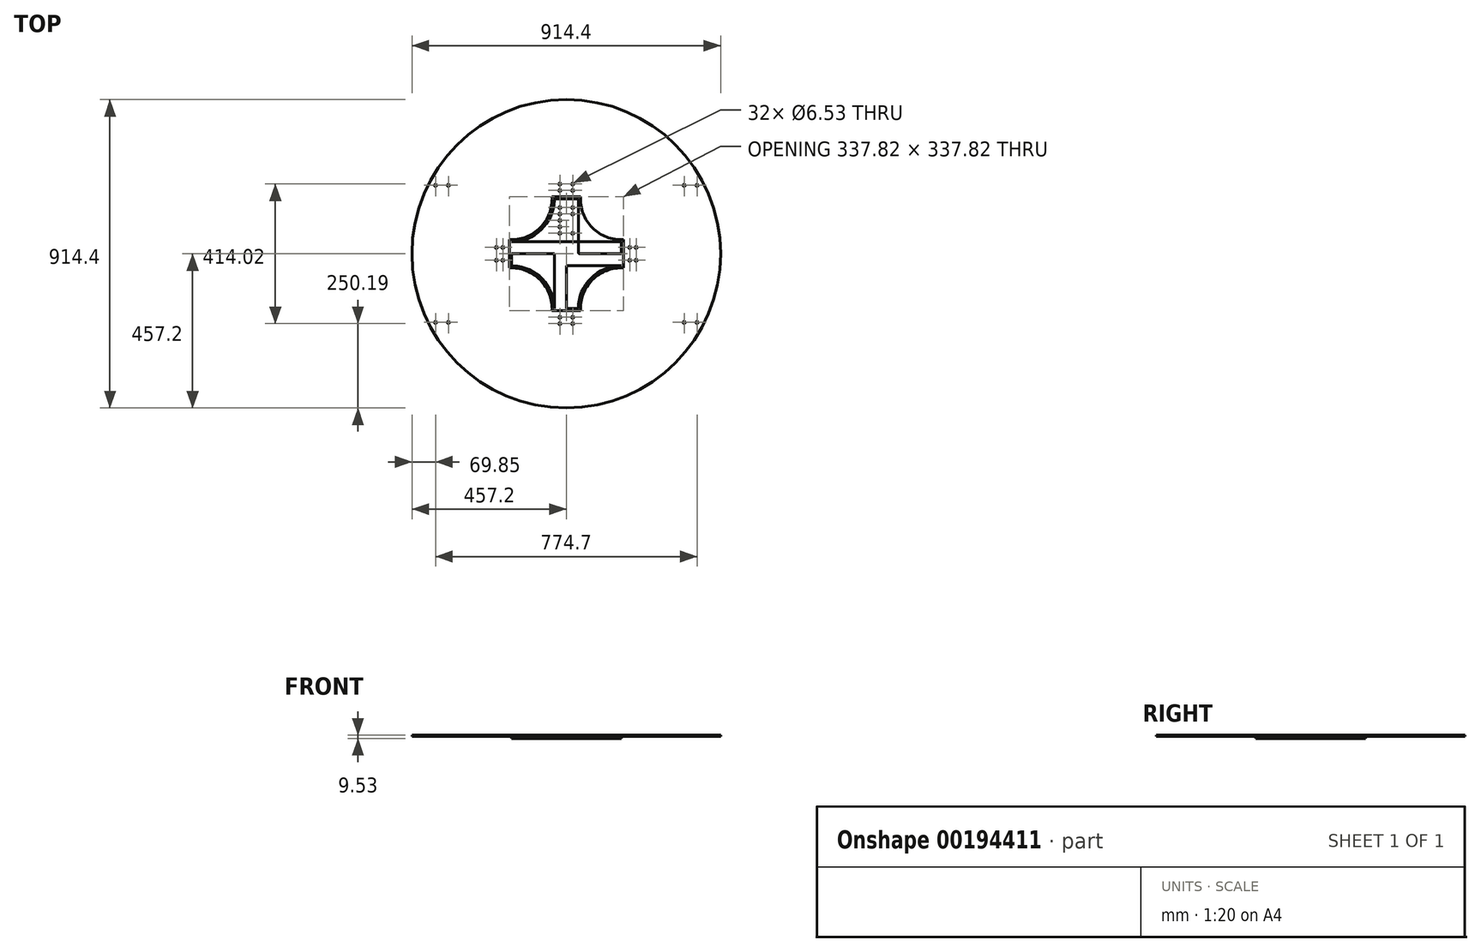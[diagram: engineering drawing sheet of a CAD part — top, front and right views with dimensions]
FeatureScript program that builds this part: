
annotation { "Feature Type Name" : "Feature", "Feature Type Description" : "" }
export const myFeature = defineFeature(function(context is Context, id is Id, definition is map)
    precondition{}
    {
        {
            var Q0;
            Q0=qCreatedBy(makeId("Top.planeOp"),FACE);
            var sketch = newSketch(context, id + "F0", { "sketchPlane" : qUnion([Q0])});
            skLineSegment(sketch, "E0.bottom", {"start": v(35.56, -35.56) * mm, "end": v(-35.56, -35.56) * mm});
            skLineSegment(sketch, "E0.top", {"start": v(35.56, 35.56) * mm, "end": v(-35.56, 35.56) * mm});
            skLineSegment(sketch, "E0.left", {"start": v(35.56, -35.56) * mm, "end": v(35.56, 35.56) * mm});
            skLineSegment(sketch, "E0.right", {"start": v(-35.56, -35.56) * mm, "end": v(-35.56, 35.56) * mm});
            skPoint(sketch, "E0.middle", {"position": v(0, 0) * mm});
            skLineSegment(sketch, "E1", {"start": v(0, 35.56) * mm, "end": v(0, 162.56) * mm});
            skPoint(sketch, "E1.endSnap0", {"position": v(0, 35.56) * mm});
            skLineSegment(sketch, "E2", {"start": v(0, 162.56) * mm, "end": v(-35.56, 162.56) * mm});
            skLineSegment(sketch, "E3", {"start": v(0, 162.56) * mm, "end": v(35.56, 162.56) * mm});
            skLineSegment(sketch, "E4", {"start": v(-35.56, 162.56) * mm, "end": v(-35.56, 35.56) * mm});
            skLineSegment(sketch, "E5", {"start": v(35.56, 162.56) * mm, "end": v(35.56, 35.56) * mm});
            skLineSegment(sketch, "E6", {"start": v(-35.56, 35.56) * mm, "end": v(-162.56, 35.56) * mm});
            skLineSegment(sketch, "E7", {"start": v(-35.56, 35.56) * mm, "end": v(-53.52, 53.52) * mm});
            skArc(sketch, "E8", {"start": v(-162.56, 35.56) * mm, "mid": v(-72.76, 72.76) * mm, "end": v(-35.56, 162.56) * mm});
            skLineSegment(sketch, "E9", {"start": v(0, 35.56) * mm, "end": v(0, 60.96) * mm});
            skLineSegment(sketch, "E10", {"start": v(0, 60.96) * mm, "end": v(19.05, 60.96) * mm});
            skLineSegment(sketch, "E11", {"start": v(19.05, 60.96) * mm, "end": v(19.05, 80.01) * mm});
            skLineSegment(sketch, "E12", {"start": v(19.05, 80.01) * mm, "end": v(19.05, 99.06) * mm});
            skLineSegment(sketch, "E13", {"start": v(19.05, 99.06) * mm, "end": v(19.05, 118.11) * mm});
            skLineSegment(sketch, "E14", {"start": v(19.05, 118.11) * mm, "end": v(19.05, 137.16) * mm});
            skLineSegment(sketch, "E15", {"start": v(19.05, 137.16) * mm, "end": v(19.05, 156.21) * mm});
            skLineSegment(sketch, "E16.MirrorCS", {"start": v(-19.05, 60.96) * mm, "end": v(-19.05, 80.01) * mm});
            skLineSegment(sketch, "E17.MirrorCS", {"start": v(-19.05, 80.01) * mm, "end": v(-19.05, 99.06) * mm});
            skLineSegment(sketch, "E18.MirrorCS", {"start": v(0, 60.96) * mm, "end": v(-19.05, 60.96) * mm});
            skLineSegment(sketch, "E19.MirrorCS", {"start": v(-19.05, 99.06) * mm, "end": v(-19.05, 118.11) * mm});
            skLineSegment(sketch, "E20.MirrorCS", {"start": v(-19.05, 118.11) * mm, "end": v(-19.05, 137.16) * mm});
            skLineSegment(sketch, "E21.MirrorCS", {"start": v(-19.05, 137.16) * mm, "end": v(-19.05, 156.21) * mm});
            skLineSegment(sketch, "E22.1.0", {"start": v(-80.01, -19.05) * mm, "end": v(-99.06, -19.05) * mm});
            skLineSegment(sketch, "E22.1.1", {"start": v(-60.96, 19.05) * mm, "end": v(-80.01, 19.05) * mm});
            skLineSegment(sketch, "E22.1.2", {"start": v(-80.01, 19.05) * mm, "end": v(-99.06, 19.05) * mm});
            skLineSegment(sketch, "E22.1.3", {"start": v(-60.96, -19.05) * mm, "end": v(-80.01, -19.05) * mm});
            skLineSegment(sketch, "E22.1.4", {"start": v(-118.11, 19.05) * mm, "end": v(-137.16, 19.05) * mm});
            skLineSegment(sketch, "E22.1.5", {"start": v(-80.01, 19.05) * mm, "end": v(-99.06, 19.05) * mm});
            skLineSegment(sketch, "E22.1.6", {"start": v(-162.56, 35.56) * mm, "end": v(-35.56, 35.56) * mm});
            skLineSegment(sketch, "E22.1.7", {"start": v(-35.56, -35.56) * mm, "end": v(-53.52, -53.52) * mm});
            skLineSegment(sketch, "E22.1.8", {"start": v(-137.16, 19.05) * mm, "end": v(-156.21, 19.05) * mm});
            skLineSegment(sketch, "E22.1.9", {"start": v(-35.56, -35.56) * mm, "end": v(-35.56, -162.56) * mm});
            skLineSegment(sketch, "E22.1.10", {"start": v(-162.56, -35.56) * mm, "end": v(-35.56, -35.56) * mm});
            skArc(sketch, "E22.1.11", {"start": v(-35.56, -162.56) * mm, "mid": v(-72.76, -72.76) * mm, "end": v(-162.56, -35.56) * mm});
            skLineSegment(sketch, "E22.1.12", {"start": v(-99.06, -19.05) * mm, "end": v(-118.11, -19.05) * mm});
            skLineSegment(sketch, "E22.1.13", {"start": v(-99.06, 19.05) * mm, "end": v(-118.11, 19.05) * mm});
            skLineSegment(sketch, "E22.1.14", {"start": v(-60.96, 0) * mm, "end": v(-60.96, 19.05) * mm});
            skLineSegment(sketch, "E22.1.15", {"start": v(-162.56, 0) * mm, "end": v(-162.56, 35.56) * mm});
            skLineSegment(sketch, "E22.1.16", {"start": v(-35.56, 0) * mm, "end": v(-162.56, 0) * mm});
            skLineSegment(sketch, "E22.1.17", {"start": v(-162.56, 0) * mm, "end": v(-162.56, -35.56) * mm});
            skLineSegment(sketch, "E22.1.18", {"start": v(-60.96, 0) * mm, "end": v(-60.96, -19.05) * mm});
            skLineSegment(sketch, "E22.1.19", {"start": v(-35.56, 35.56) * mm, "end": v(-35.56, -35.56) * mm});
            skLineSegment(sketch, "E22.1.20", {"start": v(-137.16, -19.05) * mm, "end": v(-156.21, -19.05) * mm});
            skLineSegment(sketch, "E22.1.21", {"start": v(-35.56, 0) * mm, "end": v(-60.96, 0) * mm});
            skLineSegment(sketch, "E22.1.22", {"start": v(-118.11, -19.05) * mm, "end": v(-137.16, -19.05) * mm});
            skPoint(sketch, "E22.1.23", {"position": v(-35.56, 0) * mm});
            skLineSegment(sketch, "E22.2.0", {"start": v(19.05, -80.01) * mm, "end": v(19.05, -99.06) * mm});
            skLineSegment(sketch, "E22.2.1", {"start": v(-19.05, -60.96) * mm, "end": v(-19.05, -80.01) * mm});
            skLineSegment(sketch, "E22.2.2", {"start": v(-19.05, -80.01) * mm, "end": v(-19.05, -99.06) * mm});
            skLineSegment(sketch, "E22.2.3", {"start": v(19.05, -60.96) * mm, "end": v(19.05, -80.01) * mm});
            skLineSegment(sketch, "E22.2.4", {"start": v(-19.05, -118.11) * mm, "end": v(-19.05, -137.16) * mm});
            skLineSegment(sketch, "E22.2.5", {"start": v(-19.05, -80.01) * mm, "end": v(-19.05, -99.06) * mm});
            skLineSegment(sketch, "E22.2.6", {"start": v(-35.56, -162.56) * mm, "end": v(-35.56, -35.56) * mm});
            skLineSegment(sketch, "E22.2.7", {"start": v(35.56, -35.56) * mm, "end": v(53.52, -53.52) * mm});
            skLineSegment(sketch, "E22.2.8", {"start": v(-19.05, -137.16) * mm, "end": v(-19.05, -156.21) * mm});
            skLineSegment(sketch, "E22.2.9", {"start": v(35.56, -35.56) * mm, "end": v(162.56, -35.56) * mm});
            skLineSegment(sketch, "E22.2.10", {"start": v(35.56, -162.56) * mm, "end": v(35.56, -35.56) * mm});
            skArc(sketch, "E22.2.11", {"start": v(162.56, -35.56) * mm, "mid": v(72.76, -72.76) * mm, "end": v(35.56, -162.56) * mm});
            skLineSegment(sketch, "E22.2.12", {"start": v(19.05, -99.06) * mm, "end": v(19.05, -118.11) * mm});
            skLineSegment(sketch, "E22.2.13", {"start": v(-19.05, -99.06) * mm, "end": v(-19.05, -118.11) * mm});
            skLineSegment(sketch, "E22.2.14", {"start": v(0, -60.96) * mm, "end": v(-19.05, -60.96) * mm});
            skLineSegment(sketch, "E22.2.15", {"start": v(0, -162.56) * mm, "end": v(-35.56, -162.56) * mm});
            skLineSegment(sketch, "E22.2.16", {"start": v(0, -35.56) * mm, "end": v(0, -162.56) * mm});
            skLineSegment(sketch, "E22.2.17", {"start": v(0, -162.56) * mm, "end": v(35.56, -162.56) * mm});
            skLineSegment(sketch, "E22.2.18", {"start": v(0, -60.96) * mm, "end": v(19.05, -60.96) * mm});
            skLineSegment(sketch, "E22.2.19", {"start": v(-35.56, -35.56) * mm, "end": v(35.56, -35.56) * mm});
            skLineSegment(sketch, "E22.2.20", {"start": v(19.05, -137.16) * mm, "end": v(19.05, -156.21) * mm});
            skLineSegment(sketch, "E22.2.21", {"start": v(0, -35.56) * mm, "end": v(0, -60.96) * mm});
            skLineSegment(sketch, "E22.2.22", {"start": v(19.05, -118.11) * mm, "end": v(19.05, -137.16) * mm});
            skPoint(sketch, "E22.2.23", {"position": v(0, -35.56) * mm});
            skLineSegment(sketch, "E22.3.0", {"start": v(80.01, 19.05) * mm, "end": v(99.06, 19.05) * mm});
            skLineSegment(sketch, "E22.3.1", {"start": v(60.96, -19.05) * mm, "end": v(80.01, -19.05) * mm});
            skLineSegment(sketch, "E22.3.2", {"start": v(80.01, -19.05) * mm, "end": v(99.06, -19.05) * mm});
            skLineSegment(sketch, "E22.3.3", {"start": v(60.96, 19.05) * mm, "end": v(80.01, 19.05) * mm});
            skLineSegment(sketch, "E22.3.4", {"start": v(118.11, -19.05) * mm, "end": v(137.16, -19.05) * mm});
            skLineSegment(sketch, "E22.3.5", {"start": v(80.01, -19.05) * mm, "end": v(99.06, -19.05) * mm});
            skLineSegment(sketch, "E22.3.6", {"start": v(162.56, -35.56) * mm, "end": v(35.56, -35.56) * mm});
            skLineSegment(sketch, "E22.3.7", {"start": v(35.56, 35.56) * mm, "end": v(53.52, 53.52) * mm});
            skLineSegment(sketch, "E22.3.8", {"start": v(137.16, -19.05) * mm, "end": v(156.21, -19.05) * mm});
            skLineSegment(sketch, "E22.3.9", {"start": v(35.56, 35.56) * mm, "end": v(35.56, 162.56) * mm});
            skLineSegment(sketch, "E22.3.10", {"start": v(162.56, 35.56) * mm, "end": v(35.56, 35.56) * mm});
            skArc(sketch, "E22.3.11", {"start": v(35.56, 162.56) * mm, "mid": v(72.76, 72.76) * mm, "end": v(162.56, 35.56) * mm});
            skLineSegment(sketch, "E22.3.12", {"start": v(99.06, 19.05) * mm, "end": v(118.11, 19.05) * mm});
            skLineSegment(sketch, "E22.3.13", {"start": v(99.06, -19.05) * mm, "end": v(118.11, -19.05) * mm});
            skLineSegment(sketch, "E22.3.14", {"start": v(60.96, 0) * mm, "end": v(60.96, -19.05) * mm});
            skLineSegment(sketch, "E22.3.15", {"start": v(162.56, 0) * mm, "end": v(162.56, -35.56) * mm});
            skLineSegment(sketch, "E22.3.16", {"start": v(35.56, 0) * mm, "end": v(162.56, 0) * mm});
            skLineSegment(sketch, "E22.3.17", {"start": v(162.56, 0) * mm, "end": v(162.56, 35.56) * mm});
            skLineSegment(sketch, "E22.3.18", {"start": v(60.96, 0) * mm, "end": v(60.96, 19.05) * mm});
            skLineSegment(sketch, "E22.3.20", {"start": v(137.16, 19.05) * mm, "end": v(156.21, 19.05) * mm});
            skLineSegment(sketch, "E22.3.21", {"start": v(35.56, 0) * mm, "end": v(60.96, 0) * mm});
            skLineSegment(sketch, "E22.3.22", {"start": v(118.11, 19.05) * mm, "end": v(137.16, 19.05) * mm});
            skPoint(sketch, "E22.3.23", {"position": v(35.56, 0) * mm});
            skSolve(sketch);
        }
        {
            var Q0;
            Q0=makeQuery(id+"F0.imprint","IMPRINT",FACE,{"disambiguationData":[TD([[makeQuery(id+"F0.imprint","IMPRINT",EDGE,{"derivedFrom":sQuery(id+"F0.wireOp",EDGE,"E1")}),1.0]])]});
            var Q1;
            Q1=makeQuery(id+"F0.imprint","IMPRINT",FACE,{"disambiguationData":[TD([[makeQuery(id+"F0.imprint","IMPRINT",EDGE,{"derivedFrom":sQuery(id+"F0.wireOp",EDGE,"E1")}),-1.0]])]});
            var Q2;
            Q2=makeQuery(id+"F0.imprint","IMPRINT",FACE,{"disambiguationData":[TD([[makeQuery(id+"F0.imprint","IMPRINT",EDGE,{"derivedFrom":sQuery(id+"F0.wireOp",EDGE,"E4")}),-1.0]])]});
            var Q3;
            Q3=makeQuery(id+"F0.imprint","IMPRINT",FACE,{"disambiguationData":[TD([[makeQuery(id+"F0.imprint","IMPRINT",EDGE,{"derivedFrom":sQuery(id+"F0.wireOp",EDGE,"E22.3.9")}),-1.0]])]});
            var Q4;
            {var subQ1=sQuery(id+"F0.wireOp",EDGE,"E22.1.6");Q4=makeQuery(id+"F0.imprint","IMPRINT",FACE,{"disambiguationData":[TD([[makeQuery(id+"F0.imprint","IMPRINT",EDGE,{"derivedFrom":subQ1}),-1.0]])]});}
            var Q5;
            {var subQ1=sQuery(id+"F0.wireOp",EDGE,"E22.1.10");Q5=makeQuery(id+"F0.imprint","IMPRINT",FACE,{"disambiguationData":[TD([[makeQuery(id+"F0.imprint","IMPRINT",EDGE,{"derivedFrom":subQ1}),1.0]])]});}
            var Q6;
            {var subQ1=sQuery(id+"F0.wireOp",EDGE,"E22.3.10");Q6=makeQuery(id+"F0.imprint","IMPRINT",FACE,{"disambiguationData":[TD([[makeQuery(id+"F0.imprint","IMPRINT",EDGE,{"derivedFrom":subQ1}),1.0]])]});}
            var Q7;
            {var subQ1=sQuery(id+"F0.wireOp",EDGE,"E22.3.6");Q7=makeQuery(id+"F0.imprint","IMPRINT",FACE,{"disambiguationData":[TD([[makeQuery(id+"F0.imprint","IMPRINT",EDGE,{"derivedFrom":subQ1}),-1.0]])]});}
            var Q8;
            Q8=makeQuery(id+"F0.imprint","IMPRINT",FACE,{"disambiguationData":[TD([[makeQuery(id+"F0.imprint","IMPRINT",EDGE,{"derivedFrom":sQuery(id+"F0.wireOp",EDGE,"E22.2.10")}),-1.0]])]});
            var Q9;
            {var subQ1=sQuery(id+"F0.wireOp",EDGE,"E22.2.10");Q9=makeQuery(id+"F0.imprint","IMPRINT",FACE,{"disambiguationData":[TD([[makeQuery(id+"F0.imprint","IMPRINT",EDGE,{"derivedFrom":subQ1}),1.0]])]});}
            var Q10;
            {var subQ1=sQuery(id+"F0.wireOp",EDGE,"E22.2.6");Q10=makeQuery(id+"F0.imprint","IMPRINT",FACE,{"disambiguationData":[TD([[makeQuery(id+"F0.imprint","IMPRINT",EDGE,{"derivedFrom":subQ1}),-1.0]])]});}
            var Q11;
            Q11=makeQuery(id+"F0.imprint","IMPRINT",FACE,{"disambiguationData":[TD([[makeQuery(id+"F0.imprint","IMPRINT",EDGE,{"derivedFrom":sQuery(id+"F0.wireOp",EDGE,"E22.1.10")}),-1.0]])]});
            extrude(context, id + "F1", {"entities" : qUnion([Q0, Q1, Q2, Q3, Q4, Q5, Q6, Q7, Q8, Q9, Q10, Q11]), "depth" : 6.35 * mm});
        }
        {
            var Q0;
            Q0=sQuery(id+"F0.wireOp",VERTEX,"E16.MirrorCS.start");
            var Q1;
            Q1=sQuery(id+"F0.wireOp",VERTEX,"E11.start");
            var Q2;
            Q2=sQuery(id+"F0.wireOp",VERTEX,"E12.start");
            var Q3;
            Q3=sQuery(id+"F0.wireOp",VERTEX,"E12.end");
            var Q4;
            Q4=sQuery(id+"F0.wireOp",VERTEX,"E14.start");
            var Q5;
            Q5=sQuery(id+"F0.wireOp",VERTEX,"E15.start");
            var Q6;
            Q6=sQuery(id+"F0.wireOp",VERTEX,"E17.MirrorCS.start");
            var Q7;
            Q7=sQuery(id+"F0.wireOp",VERTEX,"E17.MirrorCS.end");
            var Q8;
            Q8=sQuery(id+"F0.wireOp",VERTEX,"E20.MirrorCS.start");
            var Q9;
            Q9=sQuery(id+"F0.wireOp",VERTEX,"E21.MirrorCS.start");
            var Q10;
            Q10=sQuery(id+"F0.wireOp",VERTEX,"E22.3.3.start");
            var Q11;
            Q11=sQuery(id+"F0.wireOp",VERTEX,"E22.3.1.start");
            var Q12;
            Q12=sQuery(id+"F0.wireOp",VERTEX,"E22.3.3.end");
            var Q13;
            Q13=sQuery(id+"F0.wireOp",VERTEX,"E22.3.5.start");
            var Q14;
            Q14=sQuery(id+"F0.wireOp",VERTEX,"E22.3.12.start");
            var Q15;
            Q15=sQuery(id+"F0.wireOp",VERTEX,"E22.3.5.end");
            var Q16;
            Q16=sQuery(id+"F0.wireOp",VERTEX,"E22.3.22.start");
            var Q17;
            Q17=sQuery(id+"F0.wireOp",VERTEX,"E22.3.13.end");
            var Q18;
            Q18=sQuery(id+"F0.wireOp",VERTEX,"E22.3.20.start");
            var Q19;
            Q19=sQuery(id+"F0.wireOp",VERTEX,"E22.3.4.end");
            var Q20;
            Q20=sQuery(id+"F0.wireOp",VERTEX,"E22.2.3.start");
            var Q21;
            Q21=sQuery(id+"F0.wireOp",VERTEX,"E22.2.1.start");
            var Q22;
            Q22=sQuery(id+"F0.wireOp",VERTEX,"E22.2.5.start");
            var Q23;
            Q23=sQuery(id+"F0.wireOp",VERTEX,"E22.2.3.end");
            var Q24;
            Q24=sQuery(id+"F0.wireOp",VERTEX,"E22.2.13.start");
            var Q25;
            Q25=sQuery(id+"F0.wireOp",VERTEX,"E22.2.4.start");
            var Q26;
            Q26=sQuery(id+"F0.wireOp",VERTEX,"E22.2.12.start");
            var Q27;
            Q27=sQuery(id+"F0.wireOp",VERTEX,"E22.2.12.end");
            var Q28;
            Q28=sQuery(id+"F0.wireOp",VERTEX,"E22.2.4.end");
            var Q29;
            Q29=sQuery(id+"F0.wireOp",VERTEX,"E22.2.20.start");
            var Q30;
            Q30=sQuery(id+"F0.wireOp",VERTEX,"E22.1.1.start");
            var Q31;
            Q31=sQuery(id+"F0.wireOp",VERTEX,"E22.1.3.start");
            var Q32;
            Q32=sQuery(id+"F0.wireOp",VERTEX,"E22.1.2.start");
            var Q33;
            Q33=sQuery(id+"F0.wireOp",VERTEX,"E22.1.3.end");
            var Q34;
            Q34=sQuery(id+"F0.wireOp",VERTEX,"E22.1.2.end");
            var Q35;
            Q35=sQuery(id+"F0.wireOp",VERTEX,"E22.1.12.start");
            var Q36;
            Q36=sQuery(id+"F0.wireOp",VERTEX,"E22.1.4.start");
            var Q37;
            Q37=sQuery(id+"F0.wireOp",VERTEX,"E22.1.22.start");
            var Q38;
            Q38=sQuery(id+"F0.wireOp",VERTEX,"E22.1.20.start");
            var Q39;
            Q39=sQuery(id+"F0.wireOp",VERTEX,"E22.1.8.start");
            var Q40;
            Q40=makeQuery(id+"F1.opExtrude","SWEPT_BODY",BODY,{"disambiguationData":[OSD([sQuery(id+"F0.wireOp",EDGE,"E0.top"),sQuery(id+"F0.wireOp",EDGE,"E2"),sQuery(id+"F0.wireOp",EDGE,"E3"),sQuery(id+"F0.wireOp",EDGE,"E8"),sQuery(id+"F0.wireOp",EDGE,"E22.1.11"),sQuery(id+"F0.wireOp",EDGE,"E22.1.15"),sQuery(id+"F0.wireOp",EDGE,"E22.1.17"),sQuery(id+"F0.wireOp",EDGE,"E22.1.19"),sQuery(id+"F0.wireOp",EDGE,"E22.2.11"),sQuery(id+"F0.wireOp",EDGE,"E22.2.15"),sQuery(id+"F0.wireOp",EDGE,"E22.2.17"),sQuery(id+"F0.wireOp",EDGE,"E22.2.19"),sQuery(id+"F0.wireOp",EDGE,"E22.3.11"),sQuery(id+"F0.wireOp",EDGE,"E22.3.15"),sQuery(id+"F0.wireOp",EDGE,"E22.3.17"),sQuery(id+"F0.wireOp",EDGE,"E0.left")])]});
            hole(context, id + "F2", {"style" : HoleStyle.SIMPLE, "endStyle" : HoleEndStyle.THROUGH, "oppositeDirection" : true, "standardTappedOrClearance" : lookupTablePath({ "standard" : "ANSI", "fit" : "Close", "size" : "1/4", "type" : "Clearance" }), "standardBlindInLast" : lookupTablePath({ "fit" : "Close", "standard" : "ANSI", "size" : "1/4", "type" : "Clearance" }), "holeDiameter" : 6.53 * mm, "locations" : qUnion([Q0, Q1, Q2, Q3, Q4, Q5, Q6, Q7, Q8, Q9, Q10, Q11, Q12, Q13, Q14, Q15, Q16, Q17, Q18, Q19, Q20, Q21, Q22, Q23, Q24, Q25, Q26, Q27, Q28, Q29, Q30, Q31, Q32, Q33, Q34, Q35, Q36, Q37, Q38, Q39]), "scope" : qUnion([Q40]), "isTappedThrough" : true});
        }
        {
            var Q0;
            Q0=makeQuery(id+"F1.opExtrude","SWEPT_EDGE",EDGE,{"disambiguationData":[OSD([sQuery(id+"F0.wireOp",EDGE,"E22.1.10"),sQuery(id+"F0.wireOp",EDGE,"E22.1.19"),sQuery(id+"F0.wireOp",EDGE,"E22.2.6"),sQuery(id+"F0.wireOp",EDGE,"E22.2.19")])]});
            var Q1;
            Q1=makeQuery(id+"F1.opExtrude","SWEPT_EDGE",EDGE,{"disambiguationData":[OSD([sQuery(id+"F0.wireOp",EDGE,"E0.top"),sQuery(id+"F0.wireOp",EDGE,"E4"),sQuery(id+"F0.wireOp",EDGE,"E22.1.6"),sQuery(id+"F0.wireOp",EDGE,"E22.1.19")])]});
            var Q2;
            Q2=makeQuery(id+"F1.opExtrude","SWEPT_EDGE",EDGE,{"disambiguationData":[OSD([sQuery(id+"F0.wireOp",EDGE,"E0.top"),sQuery(id+"F0.wireOp",EDGE,"E22.3.9"),sQuery(id+"F0.wireOp",EDGE,"E22.3.10"),sQuery(id+"F0.wireOp",EDGE,"E0.left")])]});
            var Q3;
            Q3=makeQuery(id+"F1.opExtrude","SWEPT_EDGE",EDGE,{"disambiguationData":[OSD([sQuery(id+"F0.wireOp",EDGE,"E22.2.10"),sQuery(id+"F0.wireOp",EDGE,"E22.2.19"),sQuery(id+"F0.wireOp",EDGE,"E22.3.6"),sQuery(id+"F0.wireOp",EDGE,"E0.left")])]});
            fillet(context, id + "F3", {"entities" : qUnion([Q0, Q1, Q2, Q3]), "radius" : 5.08 * mm, "tangentPropagation" : true, "allowEdgeOverflow" : false});
        }
        {
            var Q0;
            Q0=makeQuery(id+"F1.opExtrude","CAP_FACE",FACE,{"disambiguationData":[OSD([sQuery(id+"F0.wireOp",EDGE,"E0.top"),sQuery(id+"F0.wireOp",EDGE,"E2"),sQuery(id+"F0.wireOp",EDGE,"E3"),sQuery(id+"F0.wireOp",EDGE,"E8"),sQuery(id+"F0.wireOp",EDGE,"E22.1.11"),sQuery(id+"F0.wireOp",EDGE,"E22.1.15"),sQuery(id+"F0.wireOp",EDGE,"E22.1.17"),sQuery(id+"F0.wireOp",EDGE,"E22.1.19"),sQuery(id+"F0.wireOp",EDGE,"E22.2.11"),sQuery(id+"F0.wireOp",EDGE,"E22.2.15"),sQuery(id+"F0.wireOp",EDGE,"E22.2.17"),sQuery(id+"F0.wireOp",EDGE,"E22.2.19"),sQuery(id+"F0.wireOp",EDGE,"E22.3.11"),sQuery(id+"F0.wireOp",EDGE,"E22.3.15"),sQuery(id+"F0.wireOp",EDGE,"E22.3.17"),sQuery(id+"F0.wireOp",EDGE,"E0.left")])],"isStart":false});
            var sketch = newSketch(context, id + "F4", { "sketchPlane" : qUnion([Q0])});
            skLineSegment(sketch, "E23.0", {"start": v(0, -168.9) * mm, "end": v(-42.08, -168.9) * mm});
            skLineSegment(sketch, "E23.1", {"start": v(0, 168.9) * mm, "end": v(-42.08, 168.9) * mm});
            skArc(sketch, "E23.2", {"start": v(-168.9, 42.08) * mm, "mid": v(-77.25, 77.25) * mm, "end": v(-42.08, 168.9) * mm});
            skLineSegment(sketch, "E23.3", {"start": v(-168.9, 0) * mm, "end": v(-168.9, 42.08) * mm});
            skLineSegment(sketch, "E23.4", {"start": v(-168.9, 0) * mm, "end": v(-168.9, -42.08) * mm});
            skLineSegment(sketch, "E23.5", {"start": v(0, 168.9) * mm, "end": v(42.08, 168.9) * mm});
            skArc(sketch, "E23.6", {"start": v(-42.08, -168.91) * mm, "mid": v(-77.25, -77.25) * mm, "end": v(-168.9, -42.08) * mm});
            skArc(sketch, "E23.7", {"start": v(42.08, 168.9) * mm, "mid": v(77.25, 77.25) * mm, "end": v(168.9, 42.08) * mm});
            skLineSegment(sketch, "E23.8", {"start": v(168.9, 0) * mm, "end": v(168.9, 42.08) * mm});
            skLineSegment(sketch, "E23.9", {"start": v(168.9, 0) * mm, "end": v(168.9, -42.08) * mm});
            skArc(sketch, "E23.10", {"start": v(168.9, -42.08) * mm, "mid": v(77.25, -77.25) * mm, "end": v(42.08, -168.9) * mm});
            skLineSegment(sketch, "E23.11", {"start": v(0, -168.9) * mm, "end": v(42.08, -168.9) * mm});
            skCircle(sketch, "E24", {"center": v(0, 0) * mm, "radius": 457.2 * mm});
            skLineSegment(sketch, "E25", {"start": v(0, 0) * mm, "end": v(0, 457.2) * mm});
            skLineSegment(sketch, "E26", {"start": v(0, 168.9) * mm, "end": v(19.05, 168.9) * mm});
            skLineSegment(sketch, "E27", {"start": v(19.05, 168.9) * mm, "end": v(19.05, 187.96) * mm});
            skLineSegment(sketch, "E28", {"start": v(19.05, 187.96) * mm, "end": v(19.05, 207.01) * mm});
            skLineSegment(sketch, "E29.MirrorCS", {"start": v(-19.05, 168.9) * mm, "end": v(-19.05, 187.96) * mm});
            skLineSegment(sketch, "E30.MirrorCS", {"start": v(-19.05, 187.96) * mm, "end": v(-19.05, 207.01) * mm});
            skLineSegment(sketch, "E31.1.0", {"start": v(-168.9, -19.05) * mm, "end": v(-187.96, -19.05) * mm});
            skLineSegment(sketch, "E31.1.1", {"start": v(-187.96, -19.05) * mm, "end": v(-207.01, -19.05) * mm});
            skLineSegment(sketch, "E31.1.2", {"start": v(-187.96, 19.05) * mm, "end": v(-207.01, 19.05) * mm});
            skLineSegment(sketch, "E31.1.3", {"start": v(-168.9, 19.05) * mm, "end": v(-187.96, 19.05) * mm});
            skLineSegment(sketch, "E31.2.0", {"start": v(19.05, -168.9) * mm, "end": v(19.05, -187.96) * mm});
            skLineSegment(sketch, "E31.2.1", {"start": v(19.05, -187.96) * mm, "end": v(19.05, -207.01) * mm});
            skLineSegment(sketch, "E31.2.2", {"start": v(-19.05, -187.96) * mm, "end": v(-19.05, -207.01) * mm});
            skLineSegment(sketch, "E31.2.3", {"start": v(-19.05, -168.9) * mm, "end": v(-19.05, -187.96) * mm});
            skLineSegment(sketch, "E31.3.0", {"start": v(168.9, 19.05) * mm, "end": v(187.96, 19.05) * mm});
            skLineSegment(sketch, "E31.3.1", {"start": v(187.96, 19.05) * mm, "end": v(207.01, 19.05) * mm});
            skLineSegment(sketch, "E31.3.2", {"start": v(187.96, -19.05) * mm, "end": v(207.01, -19.05) * mm});
            skLineSegment(sketch, "E31.3.3", {"start": v(168.9, -19.05) * mm, "end": v(187.96, -19.05) * mm});
            skSolve(sketch);
        }
        {
            var Q0;
            {var subQ5=sQuery(id+"F4.wireOp",EDGE,"E23.2");Q0=makeQuery(id+"F4.imprint","IMPRINT",FACE,{"disambiguationData":[TD([[makeQuery(id+"F4.imprint","IMPRINT",EDGE,{"derivedFrom":subQ5}),1.0]])]});}
            extrude(context, id + "F5", {"entities" : qUnion([Q0]), "depth" : 3.17 * mm});
        }
        {
            var Q0;
            Q0=sQuery(id+"F4.wireOp",VERTEX,"E30.MirrorCS.start");
            var Q1;
            Q1=sQuery(id+"F4.wireOp",VERTEX,"E30.MirrorCS.end");
            var Q2;
            Q2=sQuery(id+"F4.wireOp",VERTEX,"E28.start");
            var Q3;
            Q3=sQuery(id+"F4.wireOp",VERTEX,"E28.end");
            var Q4;
            Q4=sQuery(id+"F4.wireOp",VERTEX,"E31.3.1.start");
            var Q5;
            Q5=sQuery(id+"F4.wireOp",VERTEX,"E31.3.1.end");
            var Q6;
            Q6=sQuery(id+"F4.wireOp",VERTEX,"E31.3.3.end");
            var Q7;
            Q7=sQuery(id+"F4.wireOp",VERTEX,"E31.3.2.end");
            var Q8;
            Q8=sQuery(id+"F4.wireOp",VERTEX,"E31.2.3.end");
            var Q9;
            Q9=sQuery(id+"F4.wireOp",VERTEX,"E31.2.1.start");
            var Q10;
            Q10=sQuery(id+"F4.wireOp",VERTEX,"E31.2.2.end");
            var Q11;
            Q11=sQuery(id+"F4.wireOp",VERTEX,"E31.2.1.end");
            var Q12;
            Q12=sQuery(id+"F4.wireOp",VERTEX,"E31.1.1.start");
            var Q13;
            Q13=sQuery(id+"F4.wireOp",VERTEX,"E31.1.3.end");
            var Q14;
            Q14=sQuery(id+"F4.wireOp",VERTEX,"E31.1.1.end");
            var Q15;
            Q15=sQuery(id+"F4.wireOp",VERTEX,"E31.1.2.end");
            var Q16;
            Q16=makeQuery(id+"F5.opExtrude","SWEPT_BODY",BODY,{"disambiguationData":[OSD([sQuery(id+"F4.wireOp",EDGE,"E23.0"),sQuery(id+"F4.wireOp",EDGE,"E23.1"),sQuery(id+"F4.wireOp",EDGE,"E23.2"),sQuery(id+"F4.wireOp",EDGE,"E23.3"),sQuery(id+"F4.wireOp",EDGE,"E23.4"),sQuery(id+"F4.wireOp",EDGE,"E23.5"),sQuery(id+"F4.wireOp",EDGE,"E23.6"),sQuery(id+"F4.wireOp",EDGE,"E23.7"),sQuery(id+"F4.wireOp",EDGE,"E23.8"),sQuery(id+"F4.wireOp",EDGE,"E23.9"),sQuery(id+"F4.wireOp",EDGE,"E23.10"),sQuery(id+"F4.wireOp",EDGE,"E23.11"),sQuery(id+"F4.wireOp",EDGE,"E24"),sQuery(id+"F4.wireOp",EDGE,"E26")])]});
            hole(context, id + "F6", {"style" : HoleStyle.SIMPLE, "endStyle" : HoleEndStyle.THROUGH, "oppositeDirection" : true, "standardTappedOrClearance" : lookupTablePath({ "standard" : "ANSI", "fit" : "Close", "size" : "1/4", "type" : "Clearance" }), "standardBlindInLast" : lookupTablePath({ "fit" : "Close", "standard" : "ANSI", "size" : "1/4", "type" : "Clearance" }), "holeDiameter" : 6.53 * mm, "locations" : qUnion([Q0, Q1, Q2, Q3, Q4, Q5, Q6, Q7, Q8, Q9, Q10, Q11, Q12, Q13, Q14, Q15]), "scope" : qUnion([Q16]), "isTappedThrough" : true});
        }
        {
            var Q0;
            Q0=makeQuery(id+"F5.opExtrude","CAP_FACE",FACE,{"disambiguationData":[OSD([sQuery(id+"F4.wireOp",EDGE,"E23.0"),sQuery(id+"F4.wireOp",EDGE,"E23.1"),sQuery(id+"F4.wireOp",EDGE,"E23.2"),sQuery(id+"F4.wireOp",EDGE,"E23.3"),sQuery(id+"F4.wireOp",EDGE,"E23.4"),sQuery(id+"F4.wireOp",EDGE,"E23.5"),sQuery(id+"F4.wireOp",EDGE,"E23.6"),sQuery(id+"F4.wireOp",EDGE,"E23.7"),sQuery(id+"F4.wireOp",EDGE,"E23.8"),sQuery(id+"F4.wireOp",EDGE,"E23.9"),sQuery(id+"F4.wireOp",EDGE,"E23.10"),sQuery(id+"F4.wireOp",EDGE,"E23.11"),sQuery(id+"F4.wireOp",EDGE,"E24"),sQuery(id+"F4.wireOp",EDGE,"E26")])],"isStart":false});
            var sketch = newSketch(context, id + "F7", { "sketchPlane" : qUnion([Q0])});
            skLineSegment(sketch, "E32", {"start": v(0, 0) * mm, "end": v(368.3, 0) * mm});
            skLineSegment(sketch, "E33", {"start": v(368.3, 0) * mm, "end": v(368.3, 203.2) * mm});
            skLineSegment(sketch, "E34", {"start": v(368.3, 203.2) * mm, "end": v(349.25, 203.2) * mm});
            skLineSegment(sketch, "E35", {"start": v(368.3, 203.2) * mm, "end": v(387.35, 203.2) * mm});
            skLineSegment(sketch, "E36.MirrorCS", {"start": v(368.3, 0) * mm, "end": v(368.3, -203.2) * mm});
            skLineSegment(sketch, "E37.MirrorCS", {"start": v(368.3, -203.2) * mm, "end": v(349.25, -203.2) * mm});
            skLineSegment(sketch, "E38.MirrorCS", {"start": v(368.3, -203.2) * mm, "end": v(387.35, -203.2) * mm});
            skLineSegment(sketch, "E39", {"start": v(0, 0) * mm, "end": v(0, 372.6) * mm});
            skLineSegment(sketch, "E40.MirrorCS", {"start": v(-368.3, 0) * mm, "end": v(-368.3, 203.2) * mm});
            skLineSegment(sketch, "E41.MirrorCS", {"start": v(-368.3, 0) * mm, "end": v(-368.3, -203.2) * mm});
            skLineSegment(sketch, "E42.MirrorCS", {"start": v(-368.3, -203.2) * mm, "end": v(-349.25, -203.2) * mm});
            skLineSegment(sketch, "E43.MirrorCS", {"start": v(-368.3, -203.2) * mm, "end": v(-387.35, -203.2) * mm});
            skLineSegment(sketch, "E44.MirrorCS", {"start": v(-368.3, 203.2) * mm, "end": v(-349.25, 203.2) * mm});
            skLineSegment(sketch, "E45.MirrorCS", {"start": v(-368.3, 203.2) * mm, "end": v(-387.35, 203.2) * mm});
            skSolve(sketch);
        }
        {
            var Q0;
            Q0=sQuery(id+"F7.wireOp",VERTEX,"E45.MirrorCS.end");
            var Q1;
            Q1=sQuery(id+"F7.wireOp",VERTEX,"E44.MirrorCS.end");
            var Q2;
            Q2=sQuery(id+"F7.wireOp",VERTEX,"E35.end");
            var Q3;
            Q3=sQuery(id+"F7.wireOp",VERTEX,"E34.end");
            var Q4;
            Q4=sQuery(id+"F7.wireOp",VERTEX,"E43.MirrorCS.end");
            var Q5;
            Q5=sQuery(id+"F7.wireOp",VERTEX,"E42.MirrorCS.end");
            var Q6;
            Q6=sQuery(id+"F7.wireOp",VERTEX,"E37.MirrorCS.end");
            var Q7;
            Q7=sQuery(id+"F7.wireOp",VERTEX,"E38.MirrorCS.end");
            var Q8;
            Q8=makeQuery(id+"F5.opExtrude","SWEPT_BODY",BODY,{"disambiguationData":[OSD([sQuery(id+"F4.wireOp",EDGE,"E23.0"),sQuery(id+"F4.wireOp",EDGE,"E23.1"),sQuery(id+"F4.wireOp",EDGE,"E23.2"),sQuery(id+"F4.wireOp",EDGE,"E23.3"),sQuery(id+"F4.wireOp",EDGE,"E23.4"),sQuery(id+"F4.wireOp",EDGE,"E23.5"),sQuery(id+"F4.wireOp",EDGE,"E23.6"),sQuery(id+"F4.wireOp",EDGE,"E23.7"),sQuery(id+"F4.wireOp",EDGE,"E23.8"),sQuery(id+"F4.wireOp",EDGE,"E23.9"),sQuery(id+"F4.wireOp",EDGE,"E23.10"),sQuery(id+"F4.wireOp",EDGE,"E23.11"),sQuery(id+"F4.wireOp",EDGE,"E24"),sQuery(id+"F4.wireOp",EDGE,"E26")])]});
            hole(context, id + "F8", {"style" : HoleStyle.SIMPLE, "endStyle" : HoleEndStyle.THROUGH, "standardTappedOrClearance" : lookupTablePath({ "standard" : "ANSI", "fit" : "Close", "size" : "1/4", "type" : "Clearance" }), "standardBlindInLast" : lookupTablePath({ "fit" : "Close", "standard" : "ANSI", "size" : "1/4", "type" : "Clearance" }), "holeDiameter" : 6.53 * mm, "locations" : qUnion([Q0, Q1, Q2, Q3, Q4, Q5, Q6, Q7]), "scope" : qUnion([Q8]), "isTappedThrough" : true});
        }
    });
